# Revit family: Faucet-Wall_Mounted-Waterworks-Flyte
name_source: partatom
category: Plumbing Fixtures
revit_build: Autodesk Revit MEP 2014 (Build: 20140709_2115(x64)
units: mm (PartAtom-declared; Revit-internal decimal feet)

## types (6) — shared parameters
ADA Compliant = Yes
Assembly Code = D2010
CW Connection = Yes
Cold Water Connector = Cold Water - Female NPT
Cold Water Diameter = 0' - 0 1/2"
Default Elevation = 2' - 10"
Domestic Water Flow Rate = 1 GPM
Fittings Hole Diameter = 0' - 1 3/8"
HW Connection = Yes
Height = 0' - 2 7/8"
Hot Water Connector = Hot Water - Female NPT
Hot Water Diameter = 0' - 0 1/2"
Keynote = 22 40 00
Manufacturer = Waterworks
Pressure = 45.00 psi
Product Documentation Link = http://assets.waterworks.com
Product Page URL = http://www.waterworks.com
Spout Reach = 0' - 7 1/2"
Supply Spread = 0' - 8"
URL = http://www.waterworks.com
Valve Material = Brass, Ceramic
Vent Connection = No
Version = 2014 - v1.0a
Warranty = http://www.waterworks.com
Waste Connection = No
Water Pressure = Max: 80psi / Min: 20psi / Recommended: 45psi
zero-valued in all types: CWFU, HWFU, WFU

## per-type parameters (varying)
| type | Code Compliance | Constraint | ControlM | Cross Handles | Description | Finish | Length | Lever Handles | Model | Model SKU | Product Name | ‌Installation Requirements or Notes |
| Lever Handles - Graphite | Code # FLLS70: CEC | 2 | 3 | No | Flyte Low Profile Three Hole Wall Mounted Lavatory Faucet with Metal Lever Handles and Valve in Graphite | Metal - Waterworks - Graphite | 1' - 2 5/16" | Yes | FLLS70 | 07-97398-21382 | Flyte Low Profile Three Hole Wall Mounted Lavatory Faucet with Metal Lever Handles | Standard flow rate is 1.2gpm (4.5 L/min) and meets State of California requirements.  Includes Valve: GULV25 |
| Lever Handles - Chrome | Code # FLLS70: CEC | 2 | 2 | No | Flyte Low Profile Three Hole Wall Mounted Lavatory Faucet with Metal Lever Handles and Valve in Chrome | Metal - Waterworks - Chrome | 1' - 2 5/16" | Yes | FLLS70 | 07-44458-85550 | Flyte Low Profile Three Hole Wall Mounted Lavatory Faucet with Metal Lever Handles | Standard flow rate is 1.2gpm (4.5 L/min) and meets State of California requirements.  Includes Valve: GULV25 |
| Lever Handles - Nickel | Code # FLLS70: CEC | 2 | 1 | No | Flyte Low Profile Three Hole Wall Mounted Lavatory Faucet with Metal Lever Handles and Valve in Nickel | Metal - Waterworks - Nickel | 1' - 2 5/16" | Yes | FLLS70 | 07-31735-89836 | Flyte Low Profile Three Hole Wall Mounted Lavatory Faucet with Metal Lever Handles | Standard flow rate is 1.2gpm (4.5 L/min) and meets State of California requirements.  Includes Valve: GULV25 |
| Cross Handles - Graphite | Code # FLLS60: CEC | 1 | 3 | Yes | Flyte Low Profile Three Hole Wall Mounted Lavatory Faucet with Metal Cross Handles and Valve in Graphite | Metal - Waterworks - Graphite | 0' - 10 3/8" | No | FLLS60 | 07-99718-26428 | Flyte Low Profile Three Hole Wall Mounted Lavatory Faucet with Metal Cross Handles | Standard flow rate is 1.2gpm (4.5 L/min) and meets State of California requirements.  Includes Valve: GULV27 |
| Cross Handles - Chrome | Code # FLLS60: CEC | 1 | 2 | Yes | Flyte Low Profile Three Hole Wall Mounted Lavatory Faucet with Metal Cross Handles and Valve in Chrome | Metal - Waterworks - Chrome | 0' - 10 3/8" | No | FLLS60 | 07-23156-90468 | Flyte Low Profile Three Hole Wall Mounted Lavatory Faucet with Metal Cross Handles | Standard flow rate is 1.2gpm (4.5 L/min) and meets State of California requirements.  Includes Valve: GULV27 |
| Cross Handles - Nickel | Code # FLLS60: CEC | 1 | 1 | Yes | Flyte Low Profile Three Hole Wall Mounted Lavatory Faucet with Metal Cross Handles and Valve in Nickel | Metal - Waterworks - Nickel | 0' - 10 3/8" | No | FLLS60 | 07-70246-92616 | Flyte Low Profile Three Hole Wall Mounted Lavatory Faucet with Metal Cross Handles | Standard flow rate is 1.2gpm (4.5 L/min) and meets State of California requirements.  Includes Valve: GULV27 |

## geometry (parser evidence)
native form markers: Sweep x3
no freeform markers — native parametric forms only
